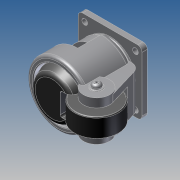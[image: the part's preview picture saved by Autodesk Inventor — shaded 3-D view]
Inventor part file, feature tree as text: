
AUTODESK INVENTOR PART (.ipt)
format: ipt  version: 2012 (Build 160160000, 160)  size: 526,848 bytes
history: native  units: mm
features: sketch x17, extrude x13, other x7, revolve x3, hole x1
ambient origin geometry x8: Origin, YZ Plane, XZ Plane, XY Plane, X Axis, Y Axis, Z Axis, Center Point
bodies: Solid1 (feature_tree)
feature tree (41):
  sketch  "Sketch_2"  dims[d3=6.0mm d4=0.0mm d5=46.0mm d6=0.0mm]
  sketch  "Sketch_1"  dims[d0=42.0mm d1=0.0mm d2=360.0deg]
  extrude  "Extrusion1"  TaperAngle=360.0deg  [1 undecoded]
  revolve  "Revolution1"  [1 undecoded]
  extrude  "Extrusion2"  Depth=45.0mm TaperAngle=0.0deg
  sketch  "Sketch_5"  dims[d14=6.0mm d15=0.0mm d16=36.0mm d17=0.0mm]
  extrude  "Extrusion3"  Depth=6.0mm TaperAngle=0.0deg
  extrude  "Extrusion4"  Depth=36.0mm TaperAngle=0.0deg
  extrude  "Extrusion5"  Depth=7.0mm TaperAngle=0.0deg
  sketch  "Sketch_6"  dims[d18=48.0mm d19=0.0mm d20=7.0mm d21=0.0mm]
  revolve  "Revolution2"  [1 undecoded]
  extrude  "Extrusion6"  Depth=2.0mm TaperAngle=0.0deg
  extrude  "Extrusion7"  [1 undecoded]
  extrude  "Extrusion8"  [1 undecoded]
  extrude  "Extrusion9"  [1 undecoded]
  extrude  "Extrusion10"  [1 undecoded]
  extrude  "Extrusion11"  [1 undecoded]
  extrude  "Extrusion12"  [1 undecoded]
  hole  "Drilling 1"  [1 undecoded]
  extrude  "Extrusion13"  [1 undecoded]
  revolve  "Revolution3"  [1 undecoded]
  other  "start_XY"
  other  "start_YZ"
  other  "start_ZX"
  other  "start_X"
  other  "start_Y"
  other  "start_Z"
  other  "start_Center"
  sketch  "Sketch_3"  dims[d7=84.0mm d8=0.0mm d9=45.0mm d10=0.0mm]
  sketch  "Sketch_4"  dims[d11=360.0deg d12=6.0mm d13=0.0mm]
  sketch  "Sketch_7"  dims[d22=8.0mm d23=0.0mm d24=28.0mm d25=0.0mm]
  sketch  "Sketch_8"  dims[d26=14.5mm d27=6.0mm d28=4.0mm d29=2.0mm d30=90.0deg d31=19.0mm d32=0.0mm d33=2.0mm d34=0.0mm]
  sketch  "Sketch_9"  dims[d35=360.0deg]
  sketch  "Sketch_10"
  sketch  "Sketch_11"
  sketch  "Sketch_12"
  sketch  "Sketch_13"
  sketch  "Sketch_14"
  sketch  "Sketch_15"
  sketch  "Sketch16"
  sketch  "Sketch_17"
note: 12 required parameter values undecoded (feature->parameter linkage not recoverable at this tier; creation-order binding heuristic only, values carry confidence <= 0.55)